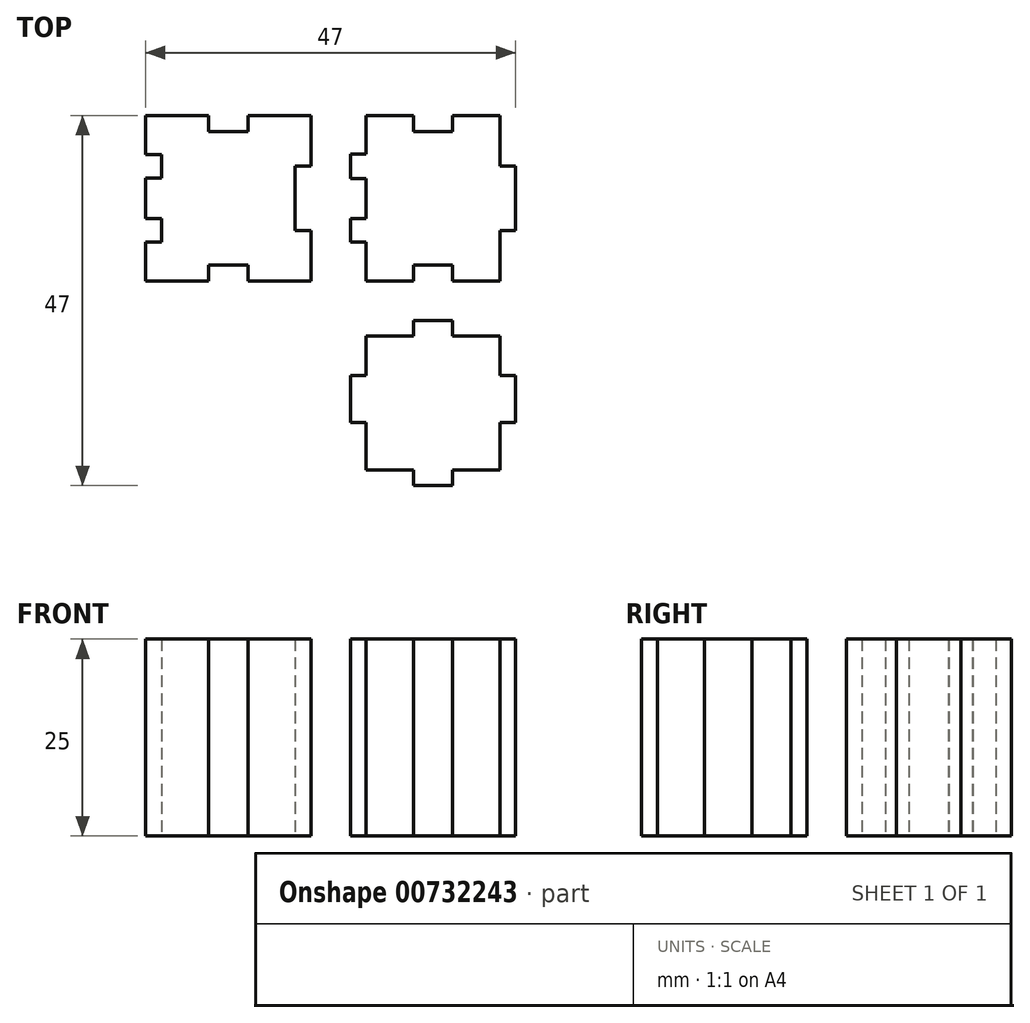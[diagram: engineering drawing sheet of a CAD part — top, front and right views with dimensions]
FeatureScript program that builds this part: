
annotation { "Feature Type Name" : "Feature", "Feature Type Description" : "" }
export const myFeature = defineFeature(function(context is Context, id is Id, definition is map)
    precondition{}
    {
        {
            var Q0;
            Q0=qCreatedBy(makeId("Top.planeOp"),FACE);
            var sketch = newSketch(context, id + "F0", { "sketchPlane" : qUnion([Q0])});
            skLineSegment(sketch, "E0", {"start": v(-26.04, 18.49) * mm, "end": v(-26.04, 13.54) * mm});
            skLineSegment(sketch, "E1", {"start": v(-26.04, 13.54) * mm, "end": v(-24.04, 13.54) * mm});
            skLineSegment(sketch, "E2", {"start": v(-24.04, 13.54) * mm, "end": v(-24.04, 10.54) * mm});
            skLineSegment(sketch, "E3", {"start": v(-24.04, 10.54) * mm, "end": v(-26.04, 10.54) * mm});
            skLineSegment(sketch, "E4", {"start": v(-26.04, 10.54) * mm, "end": v(-26.04, 5.44) * mm});
            skLineSegment(sketch, "E5", {"start": v(-26.04, 5.44) * mm, "end": v(-24.04, 5.44) * mm});
            skLineSegment(sketch, "E6", {"start": v(-24.04, 5.44) * mm, "end": v(-24.04, 2.44) * mm});
            skLineSegment(sketch, "E7", {"start": v(-24.04, 2.44) * mm, "end": v(-26.04, 2.44) * mm});
            skLineSegment(sketch, "E8", {"start": v(-26.04, 2.44) * mm, "end": v(-26.04, -2.51) * mm});
            skLineSegment(sketch, "E9", {"start": v(-5.04, -2.51) * mm, "end": v(-5.04, 3.89) * mm});
            skLineSegment(sketch, "E10", {"start": v(-5.04, 3.89) * mm, "end": v(-7.04, 3.89) * mm});
            skLineSegment(sketch, "E11", {"start": v(-7.04, 3.89) * mm, "end": v(-7.04, 12.09) * mm});
            skLineSegment(sketch, "E12", {"start": v(-7.04, 12.09) * mm, "end": v(-5.04, 12.09) * mm});
            skLineSegment(sketch, "E13", {"start": v(-5.04, 12.09) * mm, "end": v(-5.04, 18.49) * mm});
            skLineSegment(sketch, "E14", {"start": v(1.96, 18.49) * mm, "end": v(1.96, 13.59) * mm});
            skLineSegment(sketch, "E15", {"start": v(1.96, 13.59) * mm, "end": v(-0.04, 13.59) * mm});
            skLineSegment(sketch, "E16", {"start": v(-0.04, 13.59) * mm, "end": v(-0.04, 10.49) * mm});
            skLineSegment(sketch, "E17", {"start": v(-0.04, 10.49) * mm, "end": v(1.96, 10.49) * mm});
            skLineSegment(sketch, "E18", {"start": v(1.96, 10.49) * mm, "end": v(1.96, 5.44) * mm});
            skLineSegment(sketch, "E19", {"start": v(1.96, 5.44) * mm, "end": v(-0.04, 5.44) * mm});
            skLineSegment(sketch, "E20", {"start": v(-0.04, 5.44) * mm, "end": v(-0.04, 2.44) * mm});
            skLineSegment(sketch, "E21", {"start": v(-0.04, 2.44) * mm, "end": v(1.96, 2.44) * mm});
            skLineSegment(sketch, "E22", {"start": v(1.96, 2.44) * mm, "end": v(1.96, -2.51) * mm});
            skLineSegment(sketch, "E23", {"start": v(18.96, -2.51) * mm, "end": v(18.96, 3.89) * mm});
            skLineSegment(sketch, "E24", {"start": v(18.96, 3.89) * mm, "end": v(20.96, 3.89) * mm});
            skLineSegment(sketch, "E25", {"start": v(20.96, 3.89) * mm, "end": v(20.96, 12.09) * mm});
            skLineSegment(sketch, "E26", {"start": v(20.96, 12.09) * mm, "end": v(18.96, 12.09) * mm});
            skLineSegment(sketch, "E27", {"start": v(18.96, 12.09) * mm, "end": v(18.96, 18.49) * mm});
            skLineSegment(sketch, "E28", {"start": v(-18.04, 18.49) * mm, "end": v(-18.04, 16.49) * mm});
            skLineSegment(sketch, "E29", {"start": v(-18.04, 16.49) * mm, "end": v(-13.04, 16.49) * mm});
            skLineSegment(sketch, "E30", {"start": v(-13.04, 16.49) * mm, "end": v(-13.04, 18.49) * mm});
            skLineSegment(sketch, "E31", {"start": v(-26.04, 18.49) * mm, "end": v(-18.04, 18.49) * mm});
            skLineSegment(sketch, "E32", {"start": v(-13.04, 18.49) * mm, "end": v(-5.04, 18.49) * mm});
            skLineSegment(sketch, "E33", {"start": v(7.96, 18.49) * mm, "end": v(7.96, 16.49) * mm});
            skLineSegment(sketch, "E34", {"start": v(7.96, 16.49) * mm, "end": v(12.96, 16.49) * mm});
            skLineSegment(sketch, "E35", {"start": v(12.96, 16.49) * mm, "end": v(12.96, 18.49) * mm});
            skLineSegment(sketch, "E36", {"start": v(1.96, 18.49) * mm, "end": v(7.96, 18.49) * mm});
            skLineSegment(sketch, "E37", {"start": v(12.96, 18.49) * mm, "end": v(18.96, 18.49) * mm});
            skLineSegment(sketch, "E38", {"start": v(-18.04, -2.51) * mm, "end": v(-18.04, -0.51) * mm});
            skLineSegment(sketch, "E39", {"start": v(-18.04, -0.51) * mm, "end": v(-13.04, -0.51) * mm});
            skLineSegment(sketch, "E40", {"start": v(-13.04, -0.51) * mm, "end": v(-13.04, -2.51) * mm});
            skLineSegment(sketch, "E41", {"start": v(-26.04, -2.51) * mm, "end": v(-18.04, -2.51) * mm});
            skLineSegment(sketch, "E42", {"start": v(-13.04, -2.51) * mm, "end": v(-5.04, -2.51) * mm});
            skLineSegment(sketch, "E43", {"start": v(7.96, -2.51) * mm, "end": v(7.96, -0.51) * mm});
            skPoint(sketch, "E43.endSnap0", {"position": v(-15.54, -0.51) * mm});
            skLineSegment(sketch, "E44", {"start": v(7.96, -0.51) * mm, "end": v(12.96, -0.51) * mm});
            skLineSegment(sketch, "E45", {"start": v(12.96, -0.51) * mm, "end": v(12.96, -2.51) * mm});
            skLineSegment(sketch, "E46", {"start": v(1.96, -2.51) * mm, "end": v(7.96, -2.51) * mm});
            skLineSegment(sketch, "E47", {"start": v(12.96, -2.51) * mm, "end": v(18.96, -2.51) * mm});
            skLineSegment(sketch, "E48", {"start": v(1.96, -9.51) * mm, "end": v(7.96, -9.51) * mm});
            skLineSegment(sketch, "E49", {"start": v(7.96, -9.51) * mm, "end": v(7.96, -7.51) * mm});
            skLineSegment(sketch, "E50", {"start": v(7.96, -7.51) * mm, "end": v(12.96, -7.51) * mm});
            skLineSegment(sketch, "E51", {"start": v(12.96, -7.51) * mm, "end": v(12.96, -9.51) * mm});
            skLineSegment(sketch, "E52", {"start": v(12.96, -9.51) * mm, "end": v(18.96, -9.51) * mm});
            skLineSegment(sketch, "E53", {"start": v(18.96, -9.51) * mm, "end": v(18.96, -14.51) * mm});
            skLineSegment(sketch, "E54", {"start": v(18.96, -14.51) * mm, "end": v(20.96, -14.51) * mm});
            skLineSegment(sketch, "E55", {"start": v(20.96, -14.51) * mm, "end": v(20.96, -20.51) * mm});
            skLineSegment(sketch, "E56", {"start": v(20.96, -20.51) * mm, "end": v(18.96, -20.51) * mm});
            skLineSegment(sketch, "E57", {"start": v(18.96, -20.51) * mm, "end": v(18.96, -26.51) * mm});
            skLineSegment(sketch, "E58", {"start": v(18.96, -26.51) * mm, "end": v(12.96, -26.51) * mm});
            skLineSegment(sketch, "E59", {"start": v(12.96, -26.51) * mm, "end": v(12.96, -28.51) * mm});
            skLineSegment(sketch, "E60", {"start": v(12.96, -28.51) * mm, "end": v(7.96, -28.51) * mm});
            skLineSegment(sketch, "E61", {"start": v(7.96, -28.51) * mm, "end": v(7.96, -26.51) * mm});
            skLineSegment(sketch, "E62", {"start": v(7.96, -26.51) * mm, "end": v(1.96, -26.51) * mm});
            skLineSegment(sketch, "E63", {"start": v(1.96, -26.51) * mm, "end": v(1.96, -20.51) * mm});
            skLineSegment(sketch, "E64", {"start": v(1.96, -20.51) * mm, "end": v(-0.04, -20.51) * mm});
            skLineSegment(sketch, "E65", {"start": v(-0.04, -20.51) * mm, "end": v(-0.04, -14.51) * mm});
            skLineSegment(sketch, "E66", {"start": v(-0.04, -14.51) * mm, "end": v(1.96, -14.51) * mm});
            skLineSegment(sketch, "E67", {"start": v(1.96, -14.51) * mm, "end": v(1.96, -9.51) * mm});
            skSolve(sketch);
        }
        {
            var Q0;
            Q0 = qSketchRegion(id + "F0", true);
            extrude(context, id + "F1", {"entities" : qUnion([Q0]), "depth" : 25 * mm, "offsetDistance" : 25 * mm});
        }
    });
